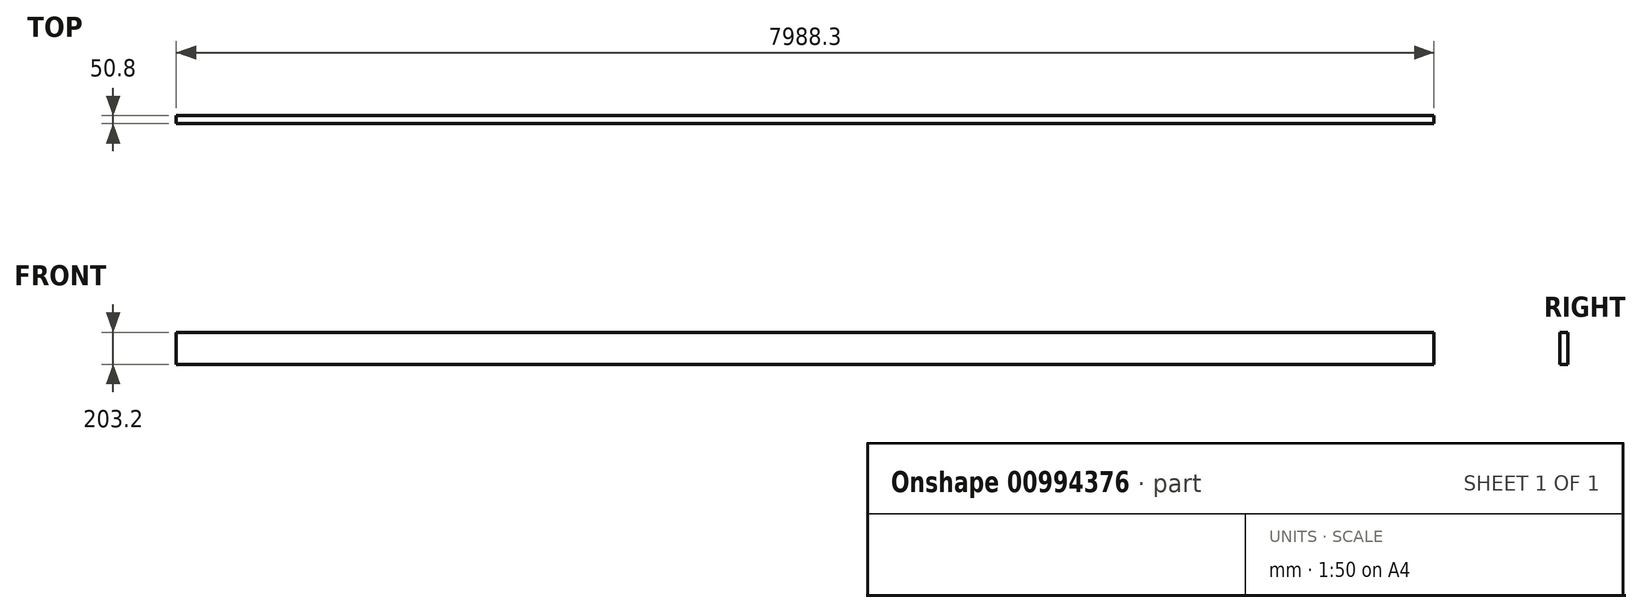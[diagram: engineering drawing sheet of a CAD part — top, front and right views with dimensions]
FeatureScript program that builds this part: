
annotation { "Feature Type Name" : "Feature", "Feature Type Description" : "" }
export const myFeature = defineFeature(function(context is Context, id is Id, definition is map)
    precondition{}
    {
        {
            var Q0;
            Q0=qCreatedBy(makeId("Front.planeOp"),FACE);
            var sketch = newSketch(context, id + "F0", { "sketchPlane" : qUnion([Q0])});
            skLineSegment(sketch, "E0.bottom", {"start": v(6526.18, 115.03) * mm, "end": v(-1462.12, 115.03) * mm});
            skLineSegment(sketch, "E0.top", {"start": v(6526.18, -88.17) * mm, "end": v(-1462.12, -88.17) * mm});
            skLineSegment(sketch, "E0.left", {"start": v(6526.18, 115.03) * mm, "end": v(6526.18, -88.17) * mm});
            skLineSegment(sketch, "E0.right", {"start": v(-1462.12, 115.03) * mm, "end": v(-1462.12, -88.17) * mm});
            skSolve(sketch);
        }
        {
            var Q0;
            Q0 = qSketchRegion(id + "F0", true);
            extrude(context, id + "F1", {"entities" : qUnion([Q0]), "depth" : 50.8 * mm, "offsetDistance" : 25.4 * mm});
        }
    });
